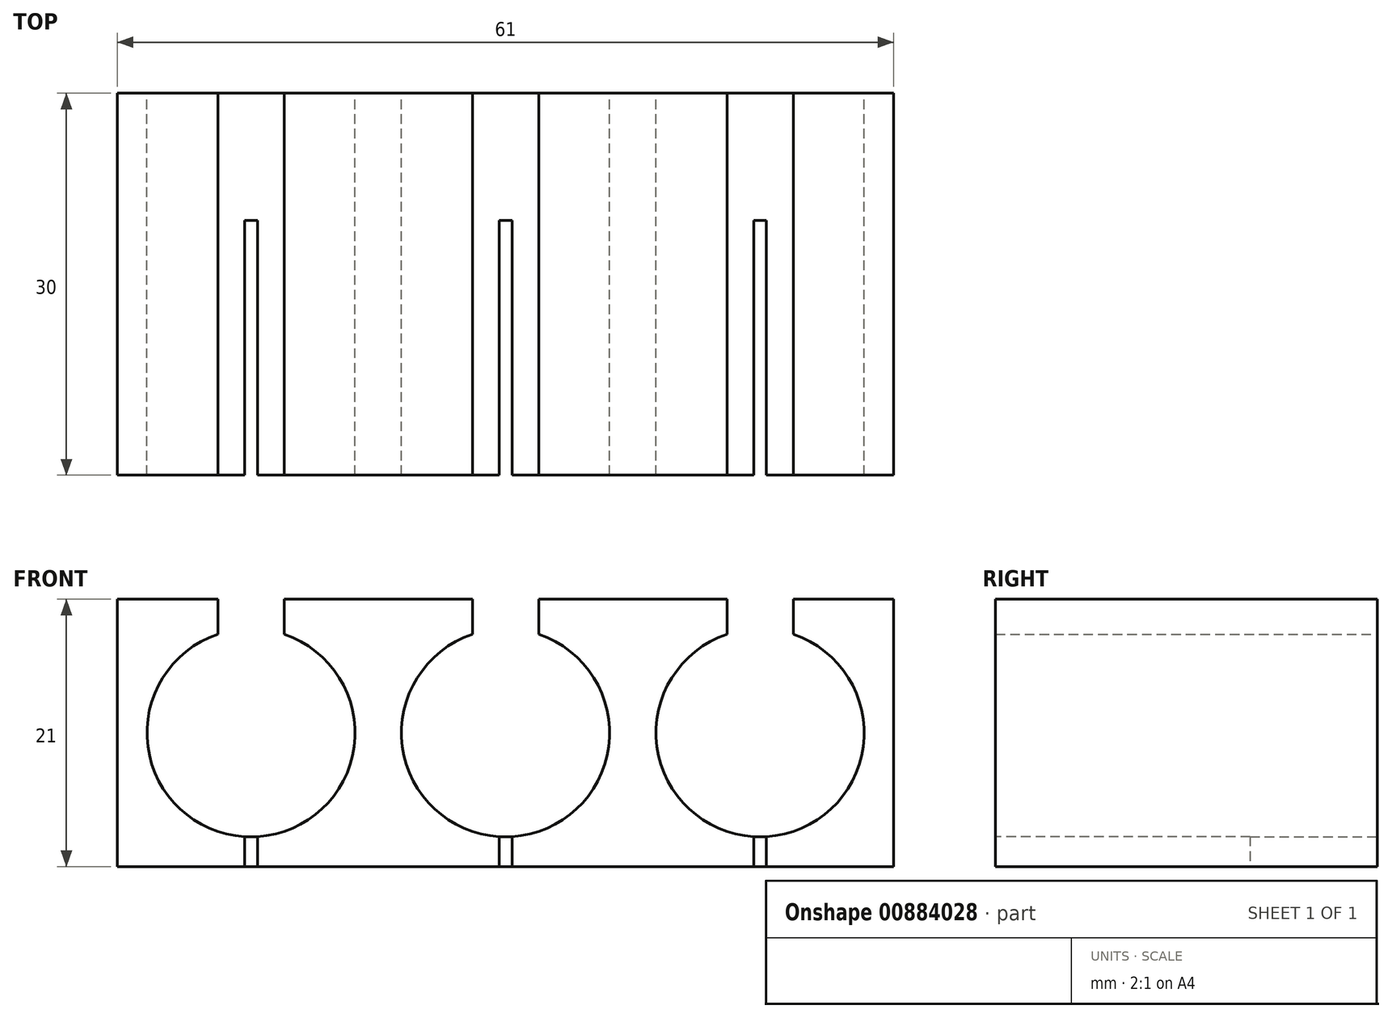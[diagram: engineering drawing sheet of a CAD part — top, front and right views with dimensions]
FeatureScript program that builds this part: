
annotation { "Feature Type Name" : "Feature", "Feature Type Description" : "" }
export const myFeature = defineFeature(function(context is Context, id is Id, definition is map)
    precondition{}
    {
        {
            var Q0;
            Q0=qCreatedBy(makeId("Front.planeOp"),FACE);
            var sketch = newSketch(context, id + "F0", { "sketchPlane" : qUnion([Q0])});
            skLineSegment(sketch, "E0.bottom", {"start": v(-47.57, 23.2) * mm, "end": v(13.43, 23.2) * mm});
            skLineSegment(sketch, "E0.top", {"start": v(-47.57, 2.2) * mm, "end": v(13.43, 2.2) * mm});
            skLineSegment(sketch, "E0.left", {"start": v(-47.57, 23.2) * mm, "end": v(-47.57, 2.2) * mm});
            skLineSegment(sketch, "E0.right", {"start": v(13.43, 23.2) * mm, "end": v(13.43, 2.2) * mm});
            skCircle(sketch, "E1", {"center": v(-37.07, 12.7) * mm, "radius": 8.18 * mm});
            skLineSegment(sketch, "E2.direction1", {"start": v(-37.07, 12.7) * mm, "end": v(-17.07, 12.7) * mm, "construction": true});
            skLineSegment(sketch, "E3", {"start": v(-17.07, 2.2) * mm, "end": v(-17.07, 23.2) * mm, "construction": true});
            skLineSegment(sketch, "E4.bottom", {"start": v(-39.67, 20.45) * mm, "end": v(-34.47, 20.45) * mm});
            skLineSegment(sketch, "E4.top", {"start": v(-39.67, 30.69) * mm, "end": v(-34.47, 30.69) * mm});
            skLineSegment(sketch, "E4.left", {"start": v(-39.67, 20.45) * mm, "end": v(-39.67, 30.69) * mm});
            skLineSegment(sketch, "E4.right", {"start": v(-34.47, 20.45) * mm, "end": v(-34.47, 30.69) * mm});
            skLineSegment(sketch, "E5.1.0.0", {"start": v(-19.67, 30.69) * mm, "end": v(-14.47, 30.69) * mm});
            skLineSegment(sketch, "E5.1.0.1", {"start": v(-14.47, 20.45) * mm, "end": v(-14.47, 30.69) * mm});
            skLineSegment(sketch, "E5.1.0.2", {"start": v(-19.67, 20.45) * mm, "end": v(-19.67, 30.69) * mm});
            skLineSegment(sketch, "E5.1.0.3", {"start": v(-19.67, 20.45) * mm, "end": v(-14.47, 20.45) * mm});
            skCircle(sketch, "E5.1.0.4", {"center": v(-17.07, 12.7) * mm, "radius": 8.18 * mm});
            skLineSegment(sketch, "E5.2.0.0", {"start": v(0.33, 30.69) * mm, "end": v(5.53, 30.69) * mm});
            skLineSegment(sketch, "E5.2.0.1", {"start": v(5.53, 20.45) * mm, "end": v(5.53, 30.69) * mm});
            skLineSegment(sketch, "E5.2.0.2", {"start": v(0.33, 20.45) * mm, "end": v(0.33, 30.69) * mm});
            skLineSegment(sketch, "E5.2.0.3", {"start": v(0.33, 20.45) * mm, "end": v(5.53, 20.45) * mm});
            skCircle(sketch, "E5.2.0.4", {"center": v(2.93, 12.7) * mm, "radius": 8.18 * mm});
            skLineSegment(sketch, "E5.direction1", {"start": v(-39.67, 30.69) * mm, "end": v(-19.67, 30.69) * mm, "construction": true});
            skPoint(sketch, "E6", {"position": v(-34.47, 25.57) * mm});
            skSolve(sketch);
        }
        {
            var Q0;
            Q0=makeQuery(id+"F0.imprint","IMPRINT",FACE,{"disambiguationData":[TD([[makeQuery(id+"F0.imprint","IMPRINT",EDGE,{"derivedFrom":sQuery(id+"F0.wireOp",EDGE,"E0.top")}),1.0]])]});
            extrude(context, id + "F1", {"entities" : qUnion([Q0]), "depth" : 30 * mm, "offsetDistance" : 25 * mm});
        }
        {
            var Q0;
            Q0=makeQuery(id+"F1.opExtrude","CAP_FACE",FACE,{"disambiguationData":[OSD([sQuery(id+"F0.wireOp",EDGE,"E0.bottom"),sQuery(id+"F0.wireOp",EDGE,"E0.top"),sQuery(id+"F0.wireOp",EDGE,"E0.left"),sQuery(id+"F0.wireOp",EDGE,"E0.right"),sQuery(id+"F0.wireOp",EDGE,"E1"),sQuery(id+"F0.wireOp",EDGE,"E4.left"),sQuery(id+"F0.wireOp",EDGE,"E4.right"),sQuery(id+"F0.wireOp",EDGE,"E5.1.0.1"),sQuery(id+"F0.wireOp",EDGE,"E5.1.0.2"),sQuery(id+"F0.wireOp",EDGE,"E5.1.0.4"),sQuery(id+"F0.wireOp",EDGE,"E5.2.0.1"),sQuery(id+"F0.wireOp",EDGE,"E5.2.0.2"),sQuery(id+"F0.wireOp",EDGE,"E5.2.0.4")])],"isStart":true});
            var sketch = newSketch(context, id + "F2", { "sketchPlane" : qUnion([Q0])});
            skLineSegment(sketch, "E7.bottom", {"start": v(-13.43, 23.2) * mm, "end": v(47.57, 23.2) * mm});
            skLineSegment(sketch, "E7.top", {"start": v(-13.43, 2.2) * mm, "end": v(47.57, 2.2) * mm});
            skLineSegment(sketch, "E7.left", {"start": v(-13.43, 23.2) * mm, "end": v(-13.43, 2.2) * mm});
            skLineSegment(sketch, "E7.right", {"start": v(47.57, 23.2) * mm, "end": v(47.57, 2.2) * mm});
            skSolve(sketch);
        }
        {
            var Q0;
            Q0=makeQuery(id+"F1.opExtrude","CAP_FACE",FACE,{"disambiguationData":[OSD([sQuery(id+"F0.wireOp",EDGE,"E0.bottom"),sQuery(id+"F0.wireOp",EDGE,"E0.top"),sQuery(id+"F0.wireOp",EDGE,"E0.left"),sQuery(id+"F0.wireOp",EDGE,"E0.right"),sQuery(id+"F0.wireOp",EDGE,"E1"),sQuery(id+"F0.wireOp",EDGE,"E4.left"),sQuery(id+"F0.wireOp",EDGE,"E4.right"),sQuery(id+"F0.wireOp",EDGE,"E5.1.0.1"),sQuery(id+"F0.wireOp",EDGE,"E5.1.0.2"),sQuery(id+"F0.wireOp",EDGE,"E5.1.0.4"),sQuery(id+"F0.wireOp",EDGE,"E5.2.0.1"),sQuery(id+"F0.wireOp",EDGE,"E5.2.0.2"),sQuery(id+"F0.wireOp",EDGE,"E5.2.0.4")])],"isStart":false});
            var sketch = newSketch(context, id + "F3", { "sketchPlane" : qUnion([Q0])});
            skLineSegment(sketch, "E8.bottom", {"start": v(-37.57, 4.54) * mm, "end": v(-36.57, 4.54) * mm});
            skLineSegment(sketch, "E8.top", {"start": v(-37.57, 2.2) * mm, "end": v(-36.57, 2.2) * mm});
            skLineSegment(sketch, "E8.left", {"start": v(-37.57, 4.54) * mm, "end": v(-37.57, 2.2) * mm});
            skLineSegment(sketch, "E8.right", {"start": v(-36.57, 4.54) * mm, "end": v(-36.57, 2.2) * mm});
            skLineSegment(sketch, "E9.bottom", {"start": v(-17.57, 4.54) * mm, "end": v(-16.57, 4.54) * mm});
            skLineSegment(sketch, "E9.top", {"start": v(-17.57, 2.2) * mm, "end": v(-16.57, 2.2) * mm});
            skLineSegment(sketch, "E9.left", {"start": v(-17.57, 4.54) * mm, "end": v(-17.57, 2.2) * mm});
            skLineSegment(sketch, "E9.right", {"start": v(-16.57, 4.54) * mm, "end": v(-16.57, 2.2) * mm});
            skLineSegment(sketch, "E10.bottom", {"start": v(2.43, 4.54) * mm, "end": v(3.43, 4.54) * mm});
            skLineSegment(sketch, "E10.top", {"start": v(2.43, 2.2) * mm, "end": v(3.43, 2.2) * mm});
            skLineSegment(sketch, "E10.left", {"start": v(2.43, 4.54) * mm, "end": v(2.43, 2.2) * mm});
            skLineSegment(sketch, "E10.right", {"start": v(3.43, 4.54) * mm, "end": v(3.43, 2.2) * mm});
            skSolve(sketch);
        }
        {
            var Q0;
            Q0 = qSketchRegion(id + "F3", true);
            extrude(context, id + "F4", {"entities" : qUnion([Q0]), "operationType" : NewBodyOperationType.REMOVE, "oppositeDirection" : true, "depth" : 20 * mm, "offsetDistance" : 25 * mm});
        }
    });
